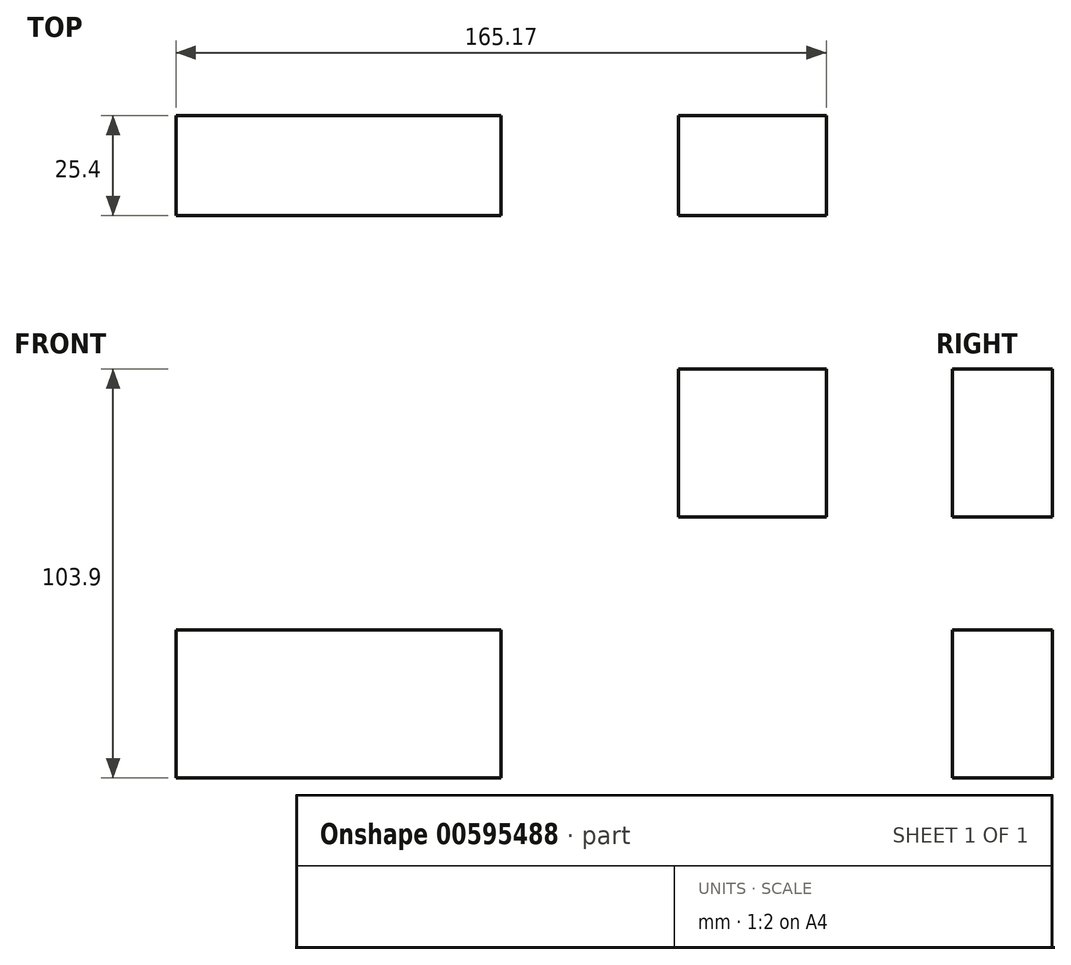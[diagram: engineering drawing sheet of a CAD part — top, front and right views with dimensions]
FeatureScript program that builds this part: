
annotation { "Feature Type Name" : "Feature", "Feature Type Description" : "" }
export const myFeature = defineFeature(function(context is Context, id is Id, definition is map)
    precondition{}
    {
        {
            var Q0;
            Q0=qCreatedBy(makeId("Front.planeOp"),FACE);
            var sketch = newSketch(context, id + "F0", { "sketchPlane" : qUnion([Q0])});
            skLineSegment(sketch, "E0.bottom", {"start": v(-41.28, 18.79) * mm, "end": v(41.28, 18.79) * mm});
            skLineSegment(sketch, "E0.top", {"start": v(-41.28, -18.79) * mm, "end": v(41.28, -18.79) * mm});
            skLineSegment(sketch, "E0.left", {"start": v(-41.28, 18.79) * mm, "end": v(-41.28, -18.79) * mm});
            skLineSegment(sketch, "E0.right", {"start": v(41.28, 18.79) * mm, "end": v(41.28, -18.79) * mm});
            skPoint(sketch, "E0.middle", {"position": v(0, 0) * mm});
            skLineSegment(sketch, "E1.bottom", {"start": v(86.36, 85.1) * mm, "end": v(123.9, 85.1) * mm});
            skLineSegment(sketch, "E1.top", {"start": v(86.36, 47.57) * mm, "end": v(123.9, 47.57) * mm});
            skLineSegment(sketch, "E1.left", {"start": v(86.36, 85.1) * mm, "end": v(86.36, 47.57) * mm});
            skLineSegment(sketch, "E1.right", {"start": v(123.9, 85.1) * mm, "end": v(123.9, 47.57) * mm});
            skPoint(sketch, "E1.middle", {"position": v(105.13, 66.34) * mm});
            skLineSegment(sketch, "E2", {"start": v(41.28, 18.79) * mm, "end": v(41.28, 42.56) * mm});
            skArc(sketch, "E3", {"start": v(41.28, 42.56) * mm, "mid": v(46.94, 53.96) * mm, "end": v(59.45, 56.33) * mm});
            skLineSegment(sketch, "E4", {"start": v(59.45, 56.33) * mm, "end": v(104.5, 56.33) * mm});
            skSolve(sketch);
        }
        {
            var Q0;
            {var subQ0=sQuery(id+"F0.wireOp",EDGE,"E1.bottom");Q0=makeQuery(id+"F0.imprint","IMPRINT",FACE,{"disambiguationData":[TD([[makeQuery(id+"F0.imprint","IMPRINT",EDGE,{"derivedFrom":subQ0}),-1.0]])]});}
            var Q1;
            Q1=makeQuery(id+"F0.imprint","IMPRINT",FACE,{"disambiguationData":[TD([[makeQuery(id+"F0.imprint","IMPRINT",EDGE,{"derivedFrom":sQuery(id+"F0.wireOp",EDGE,"E0.bottom")}),-1.0]])]});
            extrude(context, id + "F1", {"entities" : qUnion([Q0, Q1]), "depth" : 25.4 * mm, "offsetDistance" : 25.4 * mm});
        }
    });
